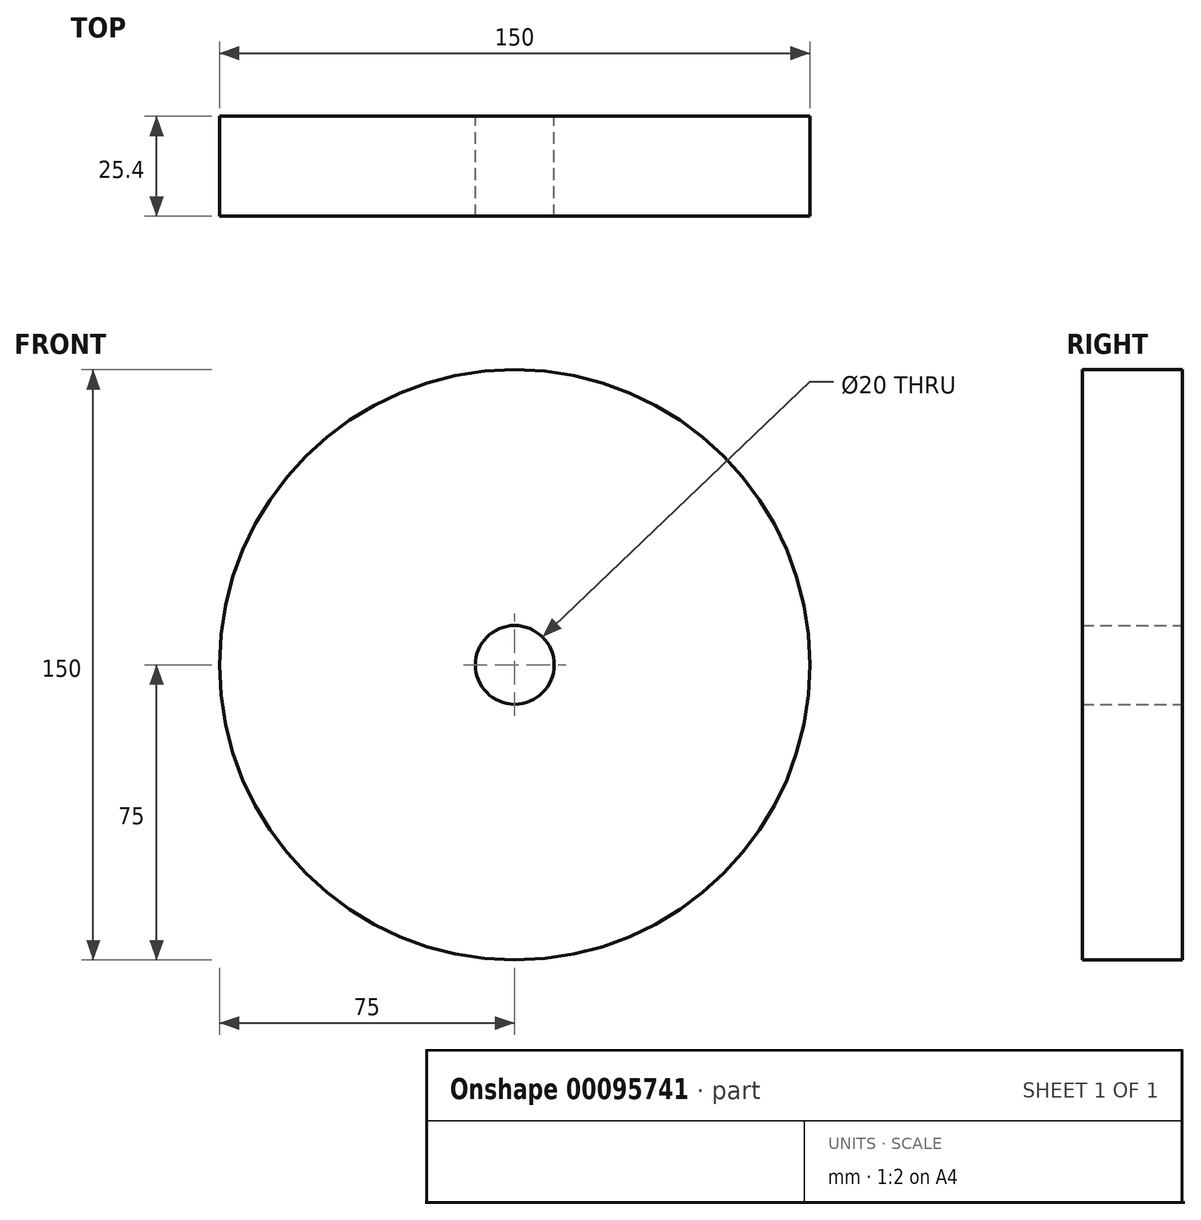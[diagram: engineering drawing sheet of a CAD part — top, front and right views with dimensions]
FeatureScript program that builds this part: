
annotation { "Feature Type Name" : "Feature", "Feature Type Description" : "" }
export const myFeature = defineFeature(function(context is Context, id is Id, definition is map)
    precondition{}
    {
        {
            var Q0;
            Q0=qCreatedBy(makeId("Front.planeOp"),FACE);
            var sketch = newSketch(context, id + "F0", { "sketchPlane" : qUnion([Q0])});
            skCircle(sketch, "E0", {"center": v(0, 0) * mm, "radius": 75 * mm});
            skCircle(sketch, "E1", {"center": v(0, 0) * mm, "radius": 10 * mm});
            skSolve(sketch);
        }
        {
            var Q0;
            Q0 = qSketchRegion(id + "F0", true);
            extrude(context, id + "F1", {"entities" : qUnion([Q0]), "endBound" : BoundingType.SYMMETRIC, "depth" : 25.4 * mm});
        }
    });
